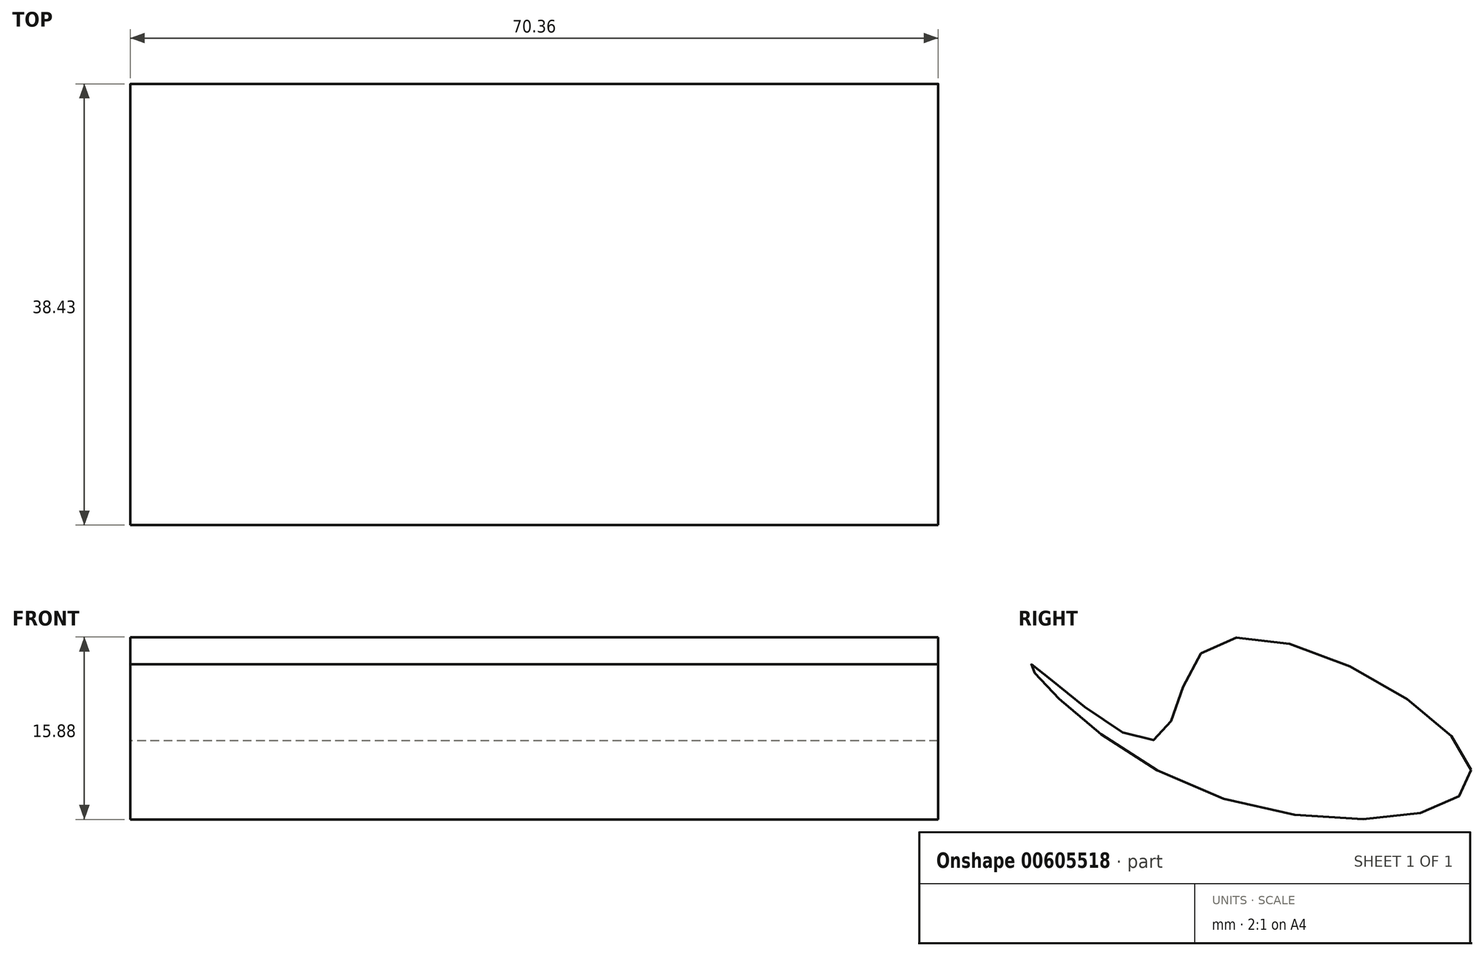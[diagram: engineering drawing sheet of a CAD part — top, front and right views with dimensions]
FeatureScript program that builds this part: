
annotation { "Feature Type Name" : "Feature", "Feature Type Description" : "" }
export const myFeature = defineFeature(function(context is Context, id is Id, definition is map)
    precondition{}
    {
        {
            var Q0;
            Q0=qCreatedBy(makeId("Right.planeOp"),FACE);
            var sketch = newSketch(context, id + "F0", { "sketchPlane" : qUnion([Q0])});
            skFitSpline(sketch, "E0", {"points": [v(13.25, 20.77) * mm, v(-8.98, 31.87) * mm, v(-14.45, 23.35) * mm, v(-24.97, 29.94) * mm, v(-10.96, 19.24) * mm, v(13.25, 20.77) * mm]});
            skSolve(sketch);
        }
        {
            var Q0;
            Q0=makeQuery(id+"F0.imprint","IMPRINT",FACE,{"disambiguationData":[TD([[makeQuery(id+"F0.imprint","IMPRINT",EDGE,{"derivedFrom":sQuery(id+"F0.wireOp",EDGE,"E0")}),1.0]])]});
            extrude(context, id + "F1", {"entities" : qUnion([Q0]), "depth" : 70.36 * mm, "offsetDistance" : 25.4 * mm});
        }
        {
            var Q0;
            Q0=makeQuery(id+"F0.imprint","IMPRINT",FACE,{"disambiguationData":[TD([[makeQuery(id+"F0.imprint","IMPRINT",EDGE,{"derivedFrom":sQuery(id+"F0.wireOp",EDGE,"E0")}),1.0]])]});
            extrude(context, id + "F2", {"entities" : qUnion([Q0]), "operationType" : NewBodyOperationType.ADD, "depth" : 25.4 * mm, "offsetDistance" : 25.4 * mm});
        }
    });
